# Revit family: Hand_Shower_Holder-GROHE-Tempesta-28605_Series
name_source: partatom
category: Specialty Equipment
units: mm (PartAtom-declared; Revit-internal decimal feet)

## family parameters
Cut with Voids When Loaded = No
Host = Face
OmniClass Number = 23.45.05.14.17
OmniClass Title = Showers
Part Type = Normal
Room Calculation Point = No
Round Connector Dimension = Use Diameter
Shared = Yes

## types (3) — shared parameters
Assembly Code = D2010710
Default Elevation = 0"
Description = WALL MOUNT HAND SHOWER HOLDER
Diameter = 1 9/16"
Installation Type = Wall Mounted
Manufacturer = Grohe
Type Comments = Non-Adjustable
URL = https://www.grohe.com
Width = 2 3/8"

## per-type parameters (varying)
| type | Finish | Material |
| 28605001 | Metal-Grohe-001-Chrome | Metal-Grohe-001-Chrome |
| 286052431 | Metal-Grohe-2431-Matte Black | Metal-Grohe-2431-Matte Black |
| 28605EN1 | Plasstic-Grohe-EN1-Brushed Nickel Infinity Finish | Plasstic-Grohe-EN1-Brushed Nickel Infinity Finish |

note: column(s) folded — value = type name in every type: Model

## geometry (parser evidence)
native form markers: Sweep x3
no freeform markers — native parametric forms only
